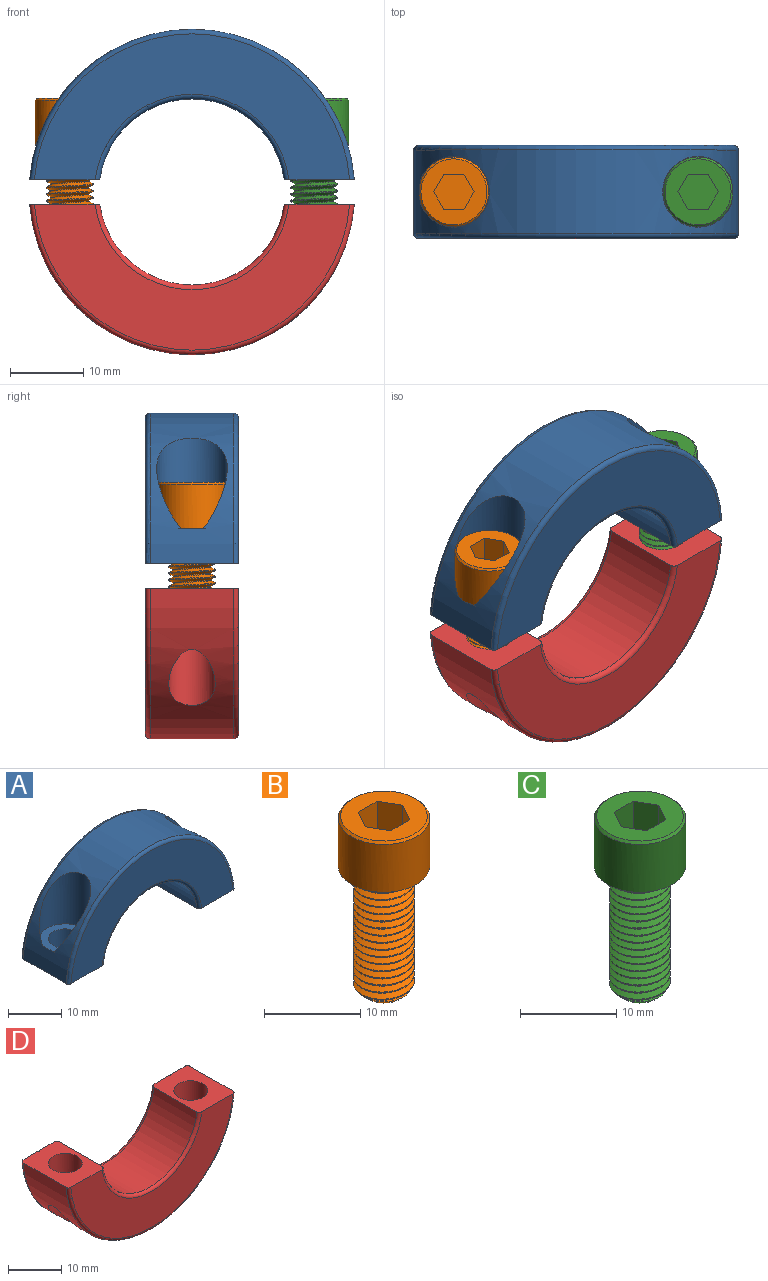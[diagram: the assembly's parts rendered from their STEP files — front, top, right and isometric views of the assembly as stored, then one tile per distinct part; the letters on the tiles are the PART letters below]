
ASSEMBLY  parts=4 mates=7
PART A: 18 faces, bbox 48x12.9x22.5 mm
  f0: plane 43.05x19.92mm, normal (0,1,0), area 229.5mm2, adj f2,f4,f7,f11
  f1: cylinder r=22.23mm len=44.33mm, axis (0,1,0), area 520.3mm2, adj f2,f4,f7,f8,f12,f13,f15,f16
  f2: plane 12.73x9.6mm, normal (0,0,-1), area 89.5mm2, adj f0,f1,f3,f5,f6,f7,f8,f9
  f3: cylinder r=12.7mm len=25.18mm, axis (0,1,0), area 417.8mm2, adj f2,f4,f9,f10
  f4: plane 12.73x9.6mm, normal (0,0,-1), area 89.5mm2, adj f0,f1,f3,f5,f6,f7,f8,f9
  f5: plane 43.05x19.92mm, normal (0,-1,0), area 425.3mm2, adj f2,f4,f8,f9
  f6: plane 34.38x15.61mm, normal (0,1,0), area 176.1mm2, adj f2,f4,f10,f11
  f7: torus R=21.59mm, axis (0,-1,0), area 65.6mm2, adj f0,f1,f2,f4
  f8: torus R=21.59mm, axis (0,-1,0), area 65.6mm2, adj f1,f2,f4,f5
  f9: torus R=13.33mm, axis (0,-1,0), area 37.2mm2, adj f2,f3,f4,f5
  f10: torus R=13.33mm, axis (0,-1,0), area 37.2mm2, adj f2,f3,f4,f6
  f11: torus R=17.46mm, axis (0,1,0), area 30.8mm2, adj f0,f2,f4,f6
  f12: plane 9.65x9.43mm, normal (0,0,1), area 41.1mm2, adj f1,f13,f14
  f13: cylinder r=4.83mm len=12.38mm, axis (0,0,-1), area 218.2mm2, adj f1,f12
  f14: cylinder r=3.17mm len=6.35mm, axis (0,0,-1), area 95mm2, adj f2,f12
  f15: cylinder r=4.83mm len=12.38mm, axis (0,0,-1), area 218.2mm2, adj f1,f16
  f16: plane 9.65x9.43mm, normal (0,0,1), area 41.1mm2, adj f1,f15,f17
  f17: cylinder r=3.17mm len=6.35mm, axis (0,0,-1), area 95mm2, adj f4,f16
PART B: 17 faces, bbox 9.9x9.9x22.7 mm
  f0: cylinder r=3.17mm len=14.97mm, axis (0,0,-1), area 37.2mm2, adj f3,f13,f14,f15
  f1: plane 9.02x9.02mm, normal (0,0,1), area 44.2mm2, adj f5,f6,f7,f8,f9,f10,f12
  f2: cylinder r=4.76mm len=9.53mm, axis (0,0,-1), area 182.4mm2, adj f3,f12
  f3: plane 9.88x9.88mm, normal (0,0,-1), area 45.1mm2, adj f0,f2,f14,f15,f16
  f4: plane 4.54x4.54mm, normal (0,0,-1), area 16.2mm2, adj f13
  f5: plane 4.76x2.75mm, normal (0,1,0), area 13.1mm2, adj f1,f6,f10,f11
  f6: plane 4.76x2.38mm, normal (0.87,0.5,0), area 13.1mm2, adj f1,f5,f7,f11
  f7: plane 4.76x2.38mm, normal (0.87,-0.5,0), area 13.1mm2, adj f1,f6,f8,f11
  f8: plane 4.76x2.75mm, normal (0,-1,0), area 13.1mm2, adj f1,f7,f9,f11
  f9: plane 4.76x2.38mm, normal (-0.87,-0.5,0), area 13.1mm2, adj f1,f8,f10,f11
  f10: plane 4.76x2.38mm, normal (-0.87,0.5,0), area 13.1mm2, adj f1,f5,f9,f11
  f11: plane 5.5x4.76mm, normal (0,0,1), area 19.6mm2, adj f5,f6,f7,f8,f9,f10
  f12: cone r=4.76mm half-angle=45deg, axis (0,0,-1), area 10.5mm2, adj f1,f2
  f13: cone r=2.27mm half-angle=45deg, axis (0,0,1), area 14.2mm2, adj f0,f4,f14,f15,f16
  f14: bspline ~16.47x6.45mm, area 206.6mm2, adj f0,f3,f13,f16
  f15: bspline ~16.02x6.45mm, area 207.1mm2, adj f0,f3,f13,f16
  f16: cylinder r=2.59mm len=15.56mm, axis (0,0,-1), area 31.4mm2, adj f3,f13,f14,f15
PART C: 17 faces, bbox 9.9x9.9x22.7 mm
  f0: cylinder r=3.17mm len=14.97mm, axis (0,0,-1), area 37.2mm2, adj f3,f13,f14,f15
  f1: plane 9.02x9.02mm, normal (0,0,1), area 44.2mm2, adj f5,f6,f7,f8,f9,f10,f12
  f2: cylinder r=4.76mm len=9.53mm, axis (0,0,-1), area 182.4mm2, adj f3,f12
  f3: plane 9.88x9.88mm, normal (0,0,-1), area 45.1mm2, adj f0,f2,f14,f15,f16
  f4: plane 4.54x4.54mm, normal (0,0,-1), area 16.2mm2, adj f13
  f5: plane 4.76x2.75mm, normal (0,1,0), area 13.1mm2, adj f1,f6,f10,f11
  f6: plane 4.76x2.38mm, normal (0.87,0.5,0), area 13.1mm2, adj f1,f5,f7,f11
  f7: plane 4.76x2.38mm, normal (0.87,-0.5,0), area 13.1mm2, adj f1,f6,f8,f11
  f8: plane 4.76x2.75mm, normal (0,-1,0), area 13.1mm2, adj f1,f7,f9,f11
  f9: plane 4.76x2.38mm, normal (-0.87,-0.5,0), area 13.1mm2, adj f1,f8,f10,f11
  f10: plane 4.76x2.38mm, normal (-0.87,0.5,0), area 13.1mm2, adj f1,f5,f9,f11
  f11: plane 5.5x4.76mm, normal (0,0,1), area 19.6mm2, adj f5,f6,f7,f8,f9,f10
  f12: cone r=4.76mm half-angle=45deg, axis (0,0,-1), area 10.5mm2, adj f1,f2
  f13: cone r=2.27mm half-angle=45deg, axis (0,0,1), area 14.2mm2, adj f0,f4,f14,f15,f16
  f14: bspline ~16.47x6.45mm, area 206.6mm2, adj f0,f3,f13,f16
  f15: bspline ~16.02x6.45mm, area 207.1mm2, adj f0,f3,f13,f16
  f16: cylinder r=2.59mm len=15.56mm, axis (0,0,-1), area 31.4mm2, adj f3,f13,f14,f15
PART D: 14 faces, bbox 48x12.9x22.5 mm
  f0: plane 43.05x19.92mm, normal (0,1,0), area 229.5mm2, adj f2,f4,f10,f11
  f1: cylinder r=22.23mm len=44.33mm, axis (0,1,0), area 661.4mm2, adj f2,f4,f7,f10,f12,f13
  f2: plane 12.73x9.6mm, normal (0,0,1), area 89.5mm2, adj f0,f1,f3,f5,f6,f7,f8,f9
  f3: cylinder r=12.7mm len=25.18mm, axis (0,1,0), area 417.8mm2, adj f2,f4,f8,f9
  f4: plane 12.73x9.6mm, normal (0,0,1), area 89.5mm2, adj f0,f1,f3,f5,f6,f7,f8,f9
  f5: plane 43.05x19.92mm, normal (0,-1,0), area 425.3mm2, adj f2,f4,f7,f8
  f6: plane 34.38x15.61mm, normal (0,1,0), area 176.1mm2, adj f2,f4,f9,f11
  f7: torus R=21.59mm, axis (0,-1,0), area 65.6mm2, adj f1,f2,f4,f5
  f8: torus R=13.33mm, axis (0,-1,0), area 37.2mm2, adj f2,f3,f4,f5
  f9: torus R=13.33mm, axis (0,-1,0), area 37.2mm2, adj f2,f3,f4,f6
  f10: torus R=21.59mm, axis (0,-1,0), area 65.6mm2, adj f0,f1,f2,f4
  f11: torus R=17.46mm, axis (0,1,0), area 30.8mm2, adj f0,f2,f4,f6
  f12: cylinder r=3.17mm len=15.99mm, axis (0,0,-1), area 251.6mm2, adj f1,f4
  f13: cylinder r=3.17mm len=15.99mm, axis (0,0,1), area 251.6mm2, adj f1,f2
PLACE A t=(-6.97,1.36,-24.01)mm
PLACE B t=(-6.97,1.36,-24.01)mm
PLACE C t=(-6.97,1.36,-24.01)mm
PLACE D t=(-6.97,1.36,-24.01)mm
MATE cylindrical B.f0 <-> A.f13  axis (0,0,-1) through (-23.64,1.36,-17.58)mm
MATE planar B.f3 <-> A.f12  axis (0,0,-1) through (-26.23,1.36,-17.58)mm
MATE planar A.f5 <-> D.f5  axis (0,-1,0) through (-6.97,-4.99,-12)mm
MATE cylindrical C.f0 <-> A.f15  axis (0,0,-1) through (9.7,1.36,-14.53)mm
MATE planar C.f3 <-> A.f16  axis (0,0,-1) through (10.96,3.97,-17.58)mm
MATE cylindrical D.f1 <-> A.f1  axis (0,1,0) through (-6.97,1.36,-24.01)mm
MATE parallel D.f4 <-> A.f2  axis (0,0,1) through (-24.35,-4.99,-25.67)mm
